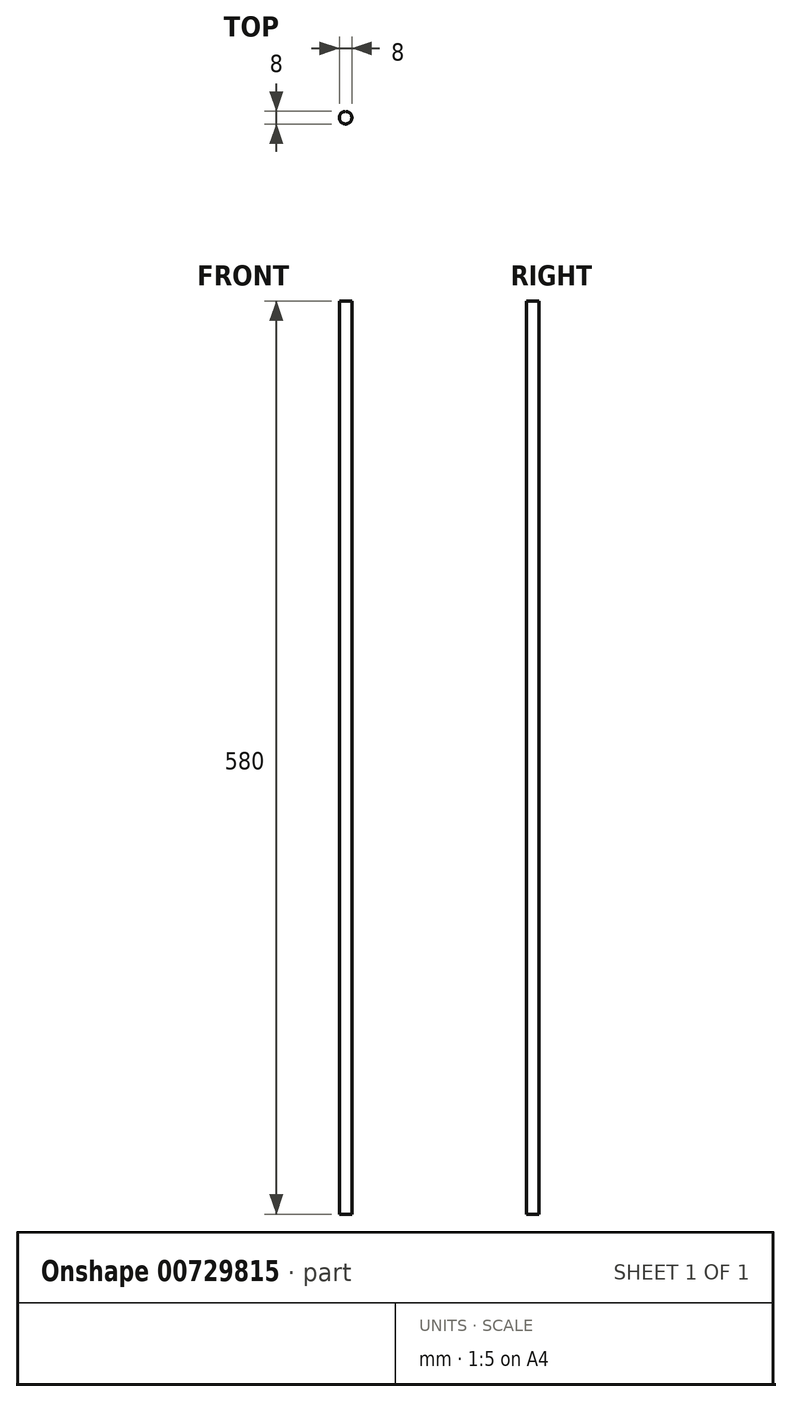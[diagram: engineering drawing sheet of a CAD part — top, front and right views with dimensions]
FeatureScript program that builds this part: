
annotation { "Feature Type Name" : "Feature", "Feature Type Description" : "" }
export const myFeature = defineFeature(function(context is Context, id is Id, definition is map)
    precondition{}
    {
        {
            var Q0;
            Q0=qCreatedBy(makeId("Top.planeOp"),FACE);
            var sketch = newSketch(context, id + "F0", { "sketchPlane" : qUnion([Q0])});
            skCircle(sketch, "E0", {"center": v(0, 0) * mm, "radius": 4 * mm});
            skSolve(sketch);
        }
        {
            var Q0;
            Q0 = qSketchRegion(id + "F0", true);
            extrude(context, id + "F1", {"entities" : qUnion([Q0]), "depth" : 580 * mm, "offsetDistance" : 25 * mm});
        }
    });
